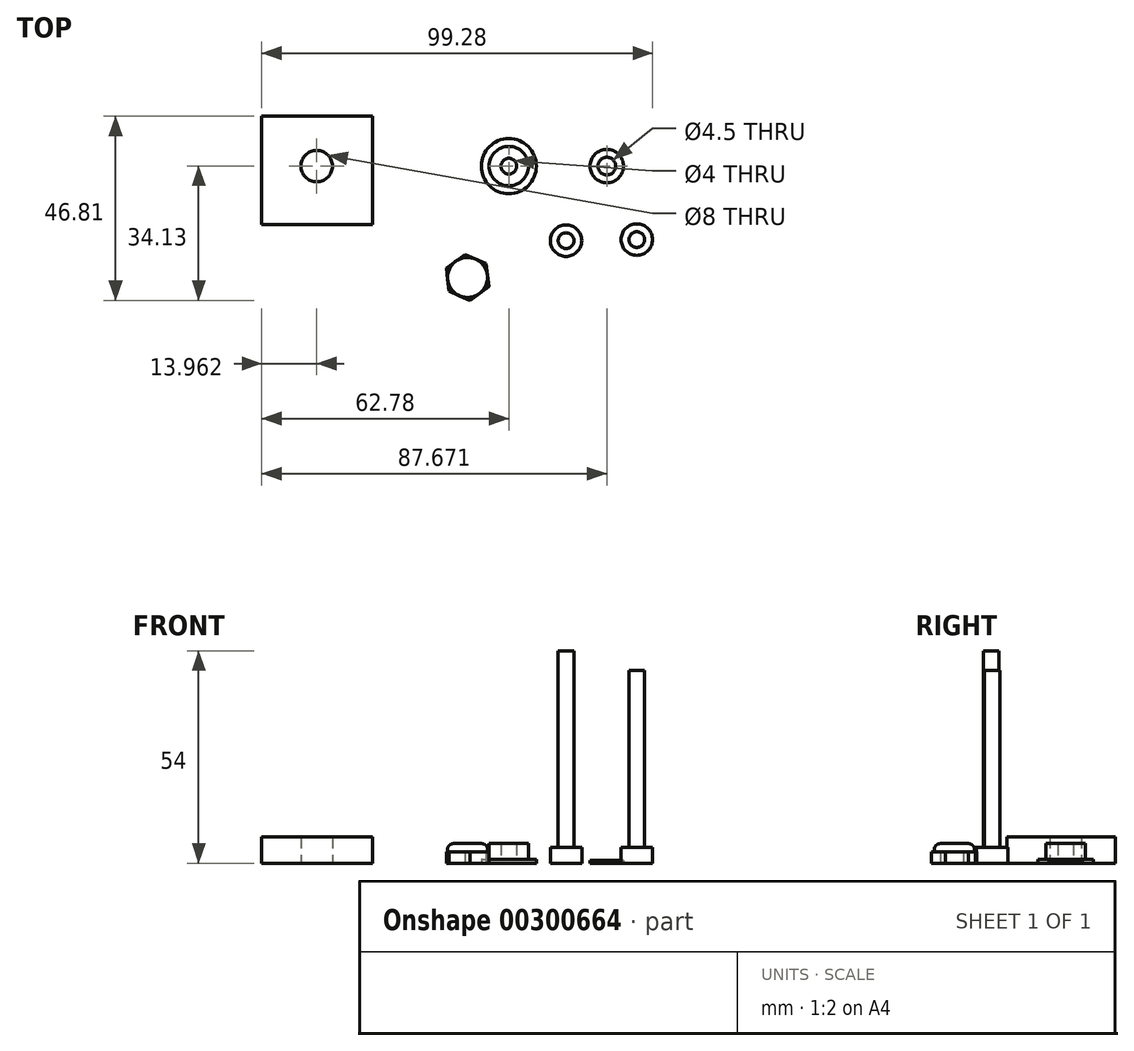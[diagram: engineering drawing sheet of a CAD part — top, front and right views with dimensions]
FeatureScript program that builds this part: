
annotation { "Feature Type Name" : "Feature", "Feature Type Description" : "" }
export const myFeature = defineFeature(function(context is Context, id is Id, definition is map)
    precondition{}
    {
        {
            var Q0;
            Q0=qCreatedBy(makeId("Top.planeOp"),FACE);
            var sketch = newSketch(context, id + "F0", { "sketchPlane" : qUnion([Q0])});
            skCircle(sketch, "E0", {"center": v(0, 0) * mm, "radius": 5 * mm});
            skCircle(sketch, "E1", {"center": v(0, 0) * mm, "radius": 7 * mm});
            skCircle(sketch, "E2", {"center": v(0, 0) * mm, "radius": 4 * mm});
            skCircle(sketch, "E3", {"center": v(0, 0) * mm, "radius": 2 * mm});
            skSolve(sketch);
        }
        {
            var Q0;
            Q0=makeQuery(id+"F0.imprint","IMPRINT",FACE,{"disambiguationData":[TD([[makeQuery(id+"F0.imprint","IMPRINT",EDGE,{"derivedFrom":sQuery(id+"F0.wireOp",EDGE,"E0")}),-1.0]])]});
            var Q1;
            Q1=makeQuery(id+"F0.imprint","IMPRINT",FACE,{"disambiguationData":[TD([[makeQuery(id+"F0.imprint","IMPRINT",EDGE,{"derivedFrom":sQuery(id+"F0.wireOp",EDGE,"E0")}),1.0]])]});
            extrude(context, id + "F1", {"entities" : qUnion([Q0, Q1]), "depth" : 1 * mm});
        }
        {
            var Q0;
            Q0=makeQuery(id+"F0.imprint","IMPRINT",FACE,{"disambiguationData":[TD([[makeQuery(id+"F0.imprint","IMPRINT",EDGE,{"derivedFrom":sQuery(id+"F0.wireOp",EDGE,"E2")}),1.0]])]});
            var Q1;
            Q1=makeQuery(id+"F0.imprint","IMPRINT",FACE,{"disambiguationData":[TD([[makeQuery(id+"F0.imprint","IMPRINT",EDGE,{"derivedFrom":sQuery(id+"F0.wireOp",EDGE,"E0")}),1.0]])]});
            extrude(context, id + "F2", {"entities" : qUnion([Q0, Q1]), "operationType" : NewBodyOperationType.ADD, "depth" : 5 * mm});
        }
        {
            var Q0;
            Q0=qCreatedBy(makeId("Top.planeOp"),FACE);
            var sketch = newSketch(context, id + "F3", { "sketchPlane" : qUnion([Q0])});
            skCircle(sketch, "E4", {"center": v(24.9, 0) * mm, "radius": 4.25 * mm});
            skCircle(sketch, "E5", {"center": v(24.9, 0) * mm, "radius": 2.25 * mm});
            skSolve(sketch);
        }
        {
            var Q0;
            Q0=makeQuery(id+"F3.imprint","IMPRINT",FACE,{"disambiguationData":[TD([[makeQuery(id+"F3.imprint","IMPRINT",EDGE,{"derivedFrom":sQuery(id+"F3.wireOp",EDGE,"E4")}),1.0]])]});
            extrude(context, id + "F4", {"entities" : qUnion([Q0]), "depth" : 0.8 * mm});
        }
        {
            var Q0;
            Q0=qCreatedBy(makeId("Top.planeOp"),FACE);
            var sketch = newSketch(context, id + "F5", { "sketchPlane" : qUnion([Q0])});
            skLineSegment(sketch, "E6.bottom", {"start": v(-62.78, 12.68) * mm, "end": v(-34.67, 12.68) * mm});
            skLineSegment(sketch, "E6.top", {"start": v(-62.78, -14.87) * mm, "end": v(-34.67, -14.87) * mm});
            skLineSegment(sketch, "E6.left", {"start": v(-62.78, 12.68) * mm, "end": v(-62.78, -14.87) * mm});
            skLineSegment(sketch, "E6.right", {"start": v(-34.67, 12.68) * mm, "end": v(-34.67, -14.87) * mm});
            skCircle(sketch, "E7", {"center": v(-48.82, 0) * mm, "radius": 4 * mm});
            skSolve(sketch);
        }
        {
            var Q0;
            Q0=makeQuery(id+"F5.imprint","IMPRINT",FACE,{"disambiguationData":[TD([[makeQuery(id+"F5.imprint","IMPRINT",EDGE,{"derivedFrom":sQuery(id+"F5.wireOp",EDGE,"E6.bottom")}),-1.0]])]});
            extrude(context, id + "F6", {"entities" : qUnion([Q0]), "depth" : 6.75 * mm});
        }
        {
            var Q0;
            Q0=qCreatedBy(makeId("Top.planeOp"),FACE);
            var sketch = newSketch(context, id + "F7", { "sketchPlane" : qUnion([Q0])});
            skCircle(sketch, "E8", {"center": v(32.5, -18.67) * mm, "radius": 4 * mm});
            skCircle(sketch, "E9", {"center": v(32.5, -18.67) * mm, "radius": 2 * mm});
            skCircle(sketch, "E10", {"center": v(14.54, -18.94) * mm, "radius": 2 * mm});
            skCircle(sketch, "E11", {"center": v(14.54, -18.94) * mm, "radius": 4 * mm});
            skSolve(sketch);
        }
        {
            var Q0;
            Q0=makeQuery(id+"F7.imprint","IMPRINT",FACE,{"disambiguationData":[TD([[makeQuery(id+"F7.imprint","IMPRINT",EDGE,{"derivedFrom":sQuery(id+"F7.wireOp",EDGE,"E8")}),1.0]])]});
            extrude(context, id + "F8", {"entities" : qUnion([Q0]), "depth" : 4 * mm});
        }
        {
            var Q0;
            Q0=makeQuery(id+"F7.imprint","IMPRINT",FACE,{"disambiguationData":[TD([[makeQuery(id+"F7.imprint","IMPRINT",EDGE,{"derivedFrom":sQuery(id+"F7.wireOp",EDGE,"E9")}),1.0]])]});
            extrude(context, id + "F9", {"entities" : qUnion([Q0]), "operationType" : NewBodyOperationType.ADD, "depth" : (45 + 4) * mm});
        }
        {
            var Q0;
            Q0=qCreatedBy(makeId("Top.planeOp"),FACE);
            var sketch = newSketch(context, id + "F10", { "sketchPlane" : qUnion([Q0])});
            skCircle(sketch, "E12.cCircle", {"center": v(-10.5, -28.29) * mm, "radius": 5.1 * mm});
            skLineSegment(sketch, "E12.0", {"start": v(-5.1, -30.62) * mm, "end": v(-9.81, -34.13) * mm});
            skLineSegment(sketch, "E12.1", {"start": v(-9.81, -34.13) * mm, "end": v(-15.21, -31.8) * mm});
            skLineSegment(sketch, "E12.2", {"start": v(-15.21, -31.8) * mm, "end": v(-15.89, -25.95) * mm});
            skLineSegment(sketch, "E12.3", {"start": v(-15.89, -25.95) * mm, "end": v(-11.17, -22.45) * mm});
            skLineSegment(sketch, "E12.4", {"start": v(-11.17, -22.45) * mm, "end": v(-5.77, -24.78) * mm});
            skLineSegment(sketch, "E12.5", {"start": v(-5.77, -24.78) * mm, "end": v(-5.1, -30.62) * mm});
            skPoint(sketch, "E12.0.midPoint", {"position": v(-7.45, -32.37) * mm});
            skSolve(sketch);
        }
        {
            var Q0;
            {var subQ0=sQuery(id+"F10.wireOp",EDGE,"E12.cCircle");var subQ4=makeQuery(id+"F10.imprint","INTERSECT",VERTEX,{"derivedFrom":[subQ0,sQuery(id+"F10.wireOp",EDGE,"E12.4")]});Q0=makeQuery(id+"F10.imprint","IMPRINT",FACE,{"disambiguationData":[TD([[makeQuery(id+"F10.imprint","IMPRINT",EDGE,{"disambiguationData":[TD([[subQ4,1.0]])],"derivedFrom":subQ0}),1.0]])]});}
            var Q1;
            {var subQ0=sQuery(id+"F10.wireOp",EDGE,"E12.2");var subQ1=sQuery(id+"F10.wireOp",EDGE,"E12.cCircle");var subQ2=makeQuery(id+"F10.imprint","INTERSECT",VERTEX,{"derivedFrom":[subQ1,subQ0]});Q1=makeQuery(id+"F10.imprint","IMPRINT",FACE,{"disambiguationData":[TD([[makeQuery(id+"F10.imprint","IMPRINT",EDGE,{"disambiguationData":[TD([[subQ2,-1.0]])],"derivedFrom":subQ1}),-1.0]])]});}
            var Q2;
            {var subQ0=sQuery(id+"F10.wireOp",EDGE,"E12.1");var subQ1=sQuery(id+"F10.wireOp",EDGE,"E12.cCircle");var subQ2=makeQuery(id+"F10.imprint","INTERSECT",VERTEX,{"derivedFrom":[subQ1,subQ0]});Q2=makeQuery(id+"F10.imprint","IMPRINT",FACE,{"disambiguationData":[TD([[makeQuery(id+"F10.imprint","IMPRINT",EDGE,{"disambiguationData":[TD([[subQ2,-1.0]])],"derivedFrom":subQ1}),-1.0]])]});}
            var Q3;
            {var subQ0=sQuery(id+"F10.wireOp",EDGE,"E12.5");var subQ1=sQuery(id+"F10.wireOp",EDGE,"E12.cCircle");var subQ2=makeQuery(id+"F10.imprint","INTERSECT",VERTEX,{"derivedFrom":[subQ1,subQ0]});Q3=makeQuery(id+"F10.imprint","IMPRINT",FACE,{"disambiguationData":[TD([[makeQuery(id+"F10.imprint","IMPRINT",EDGE,{"disambiguationData":[TD([[subQ2,1.0]])],"derivedFrom":subQ1}),-1.0]])]});}
            var Q4;
            {var subQ0=sQuery(id+"F10.wireOp",EDGE,"E12.3");var subQ1=sQuery(id+"F10.wireOp",EDGE,"E12.cCircle");var subQ2=makeQuery(id+"F10.imprint","INTERSECT",VERTEX,{"derivedFrom":[subQ1,subQ0]});Q4=makeQuery(id+"F10.imprint","IMPRINT",FACE,{"disambiguationData":[TD([[makeQuery(id+"F10.imprint","IMPRINT",EDGE,{"disambiguationData":[TD([[subQ2,-1.0]])],"derivedFrom":subQ1}),-1.0]])]});}
            var Q5;
            {var subQ0=sQuery(id+"F10.wireOp",EDGE,"E12.4");var subQ1=sQuery(id+"F10.wireOp",EDGE,"E12.cCircle");var subQ2=makeQuery(id+"F10.imprint","INTERSECT",VERTEX,{"derivedFrom":[subQ1,subQ0]});Q5=makeQuery(id+"F10.imprint","IMPRINT",FACE,{"disambiguationData":[TD([[makeQuery(id+"F10.imprint","IMPRINT",EDGE,{"disambiguationData":[TD([[subQ2,1.0]])],"derivedFrom":subQ1}),-1.0]])]});}
            var Q6;
            {var subQ0=sQuery(id+"F10.wireOp",EDGE,"E12.4");var subQ1=sQuery(id+"F10.wireOp",EDGE,"E12.cCircle");var subQ2=makeQuery(id+"F10.imprint","INTERSECT",VERTEX,{"derivedFrom":[subQ1,subQ0]});Q6=makeQuery(id+"F10.imprint","IMPRINT",FACE,{"disambiguationData":[TD([[makeQuery(id+"F10.imprint","IMPRINT",EDGE,{"disambiguationData":[TD([[subQ2,-1.0]])],"derivedFrom":subQ1}),-1.0]])]});}
            var Q7;
            Q7=sQuery(id+"F10.wireOp",EDGE,"E12.2");
            var Q8;
            Q8=sQuery(id+"F10.wireOp",EDGE,"E12.3");
            var Q9;
            Q9=sQuery(id+"F10.wireOp",EDGE,"E12.4");
            var Q10;
            Q10=sQuery(id+"F10.wireOp",EDGE,"E12.5");
            var Q11;
            Q11=sQuery(id+"F10.wireOp",EDGE,"E12.0");
            var Q12;
            Q12=sQuery(id+"F10.wireOp",EDGE,"E12.1");
            extrude(context, id + "F11", {"entities" : qUnion([Q0, Q1, Q2, Q3, Q4, Q5, Q6]), "surfaceEntities" : qUnion([Q7, Q8, Q9, Q10, Q11, Q12]), "depth" : 2.9 * mm});
        }
        {
            var Q0;
            {var subQ0=sQuery(id+"F10.wireOp",EDGE,"E12.cCircle");var subQ4=makeQuery(id+"F10.imprint","INTERSECT",VERTEX,{"derivedFrom":[subQ0,sQuery(id+"F10.wireOp",EDGE,"E12.4")]});Q0=makeQuery(id+"F10.imprint","IMPRINT",FACE,{"disambiguationData":[TD([[makeQuery(id+"F10.imprint","IMPRINT",EDGE,{"disambiguationData":[TD([[subQ4,1.0]])],"derivedFrom":subQ0}),1.0]])]});}
            extrude(context, id + "F12", {"entities" : qUnion([Q0]), "operationType" : NewBodyOperationType.ADD, "depth" : 5 * mm});
        }
        {
            var Q0;
            Q0=makeQuery(id+"F12.opExtrude","CAP_EDGE",EDGE,{"disambiguationData":[OSD([sQuery(id+"F10.wireOp",EDGE,"E12.cCircle")])],"isStart":false});
            fillet(context, id + "F13", {"entities" : qUnion([Q0]), "radius" : 1.5 * mm, "tangentPropagation" : true, "allowEdgeOverflow" : false});
        }
        {
            var Q0;
            Q0=makeQuery(id+"F7.imprint","IMPRINT",FACE,{"disambiguationData":[TD([[makeQuery(id+"F7.imprint","IMPRINT",EDGE,{"derivedFrom":sQuery(id+"F7.wireOp",EDGE,"E10")}),-1.0]])]});
            extrude(context, id + "F14", {"entities" : qUnion([Q0]), "depth" : 4 * mm});
        }
        {
            var Q0;
            Q0=makeQuery(id+"F7.imprint","IMPRINT",FACE,{"disambiguationData":[TD([[makeQuery(id+"F7.imprint","IMPRINT",EDGE,{"derivedFrom":sQuery(id+"F7.wireOp",EDGE,"E10")}),1.0]])]});
            extrude(context, id + "F15", {"entities" : qUnion([Q0]), "operationType" : NewBodyOperationType.ADD, "depth" : (50 + 4) * mm});
        }
    });
